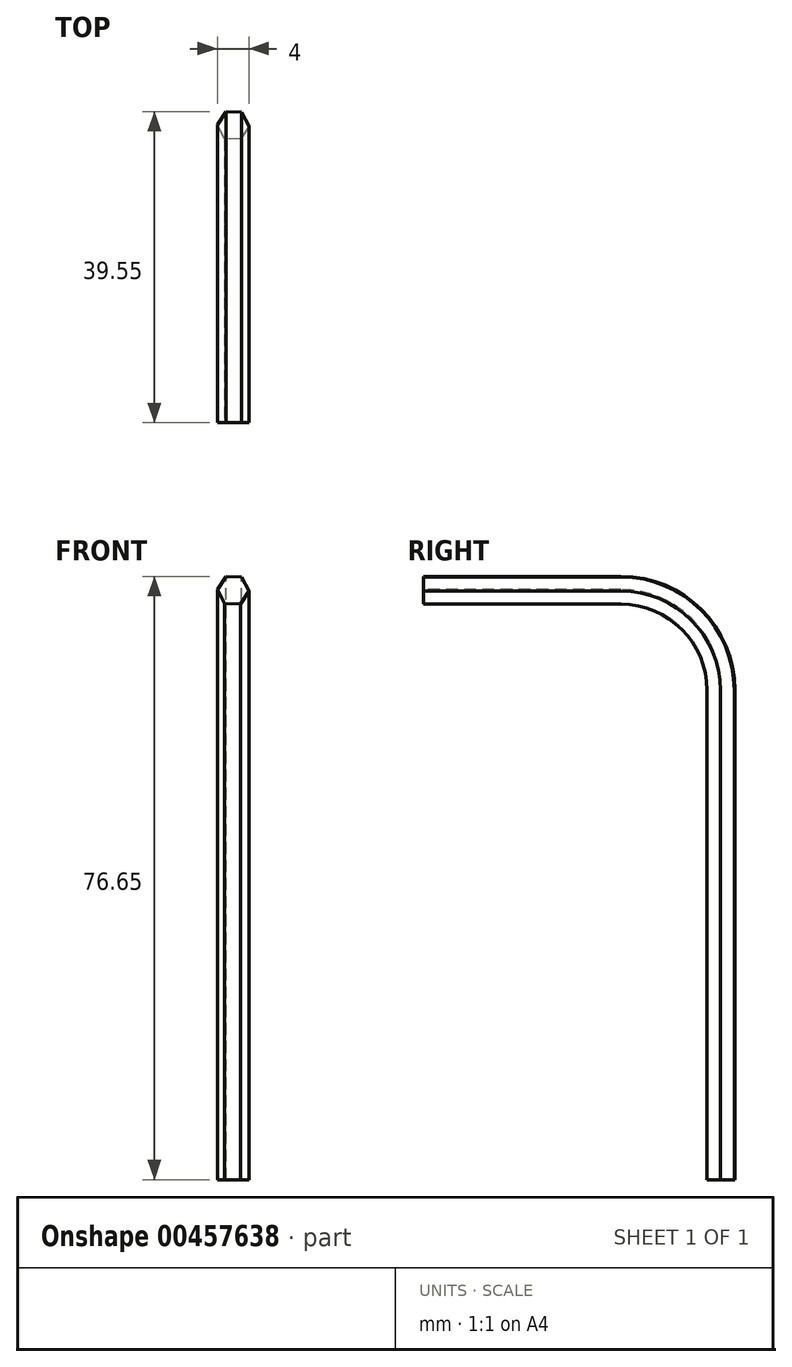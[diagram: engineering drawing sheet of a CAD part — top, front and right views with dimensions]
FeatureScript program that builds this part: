
annotation { "Feature Type Name" : "Feature", "Feature Type Description" : "" }
export const myFeature = defineFeature(function(context is Context, id is Id, definition is map)
    precondition{}
    {
        {
            var Q0;
            Q0=qCreatedBy(makeId("Top.planeOp"),FACE);
            var sketch = newSketch(context, id + "F0", { "sketchPlane" : qUnion([Q0])});
            skCircle(sketch, "E0.cCircle", {"center": v(0, 0) * mm, "radius": 1.73 * mm, "construction": true});
            skLineSegment(sketch, "E0.0", {"start": v(-1.07, -1.7) * mm, "end": v(-2, 0.08) * mm});
            skLineSegment(sketch, "E0.1", {"start": v(-2, 0.08) * mm, "end": v(-0.93, 1.77) * mm});
            skLineSegment(sketch, "E0.2", {"start": v(-0.93, 1.77) * mm, "end": v(1.07, 1.7) * mm});
            skLineSegment(sketch, "E0.3", {"start": v(1.07, 1.7) * mm, "end": v(2, -0.08) * mm});
            skLineSegment(sketch, "E0.4", {"start": v(2, -0.08) * mm, "end": v(0.93, -1.77) * mm});
            skLineSegment(sketch, "E0.5", {"start": v(0.93, -1.77) * mm, "end": v(-1.07, -1.7) * mm});
            skPoint(sketch, "E0.0.midPoint", {"position": v(-1.53, -0.8) * mm});
            skSolve(sketch);
        }
        {
            var Q0;
            Q0=qCreatedBy(makeId("Right.planeOp"),FACE);
            var sketch = newSketch(context, id + "F1", { "sketchPlane" : qUnion([Q0])});
            skLineSegment(sketch, "E1", {"start": v(0, 0) * mm, "end": v(0, 62.18) * mm});
            skLineSegment(sketch, "E2", {"start": v(-12.7, 74.88) * mm, "end": v(-37.78, 74.88) * mm});
            skPoint(sketch, "E3.visualSharp", {"position": v(0, 74.88) * mm});
            skArc(sketch, "E3.filletArc", {"start": v(0, 62.18) * mm, "mid": v(-3.72, 71.16) * mm, "end": v(-12.7, 74.88) * mm});
            skSolve(sketch);
        }
        {
            var Q0;
            Q0=makeQuery(id+"F0.imprint","IMPRINT",FACE,{"disambiguationData":[TD([[makeQuery(id+"F0.imprint","IMPRINT",EDGE,{"derivedFrom":sQuery(id+"F0.wireOp",EDGE,"E0.0")}),-1.0]])]});
            var Q1;
            Q1=sQuery(id+"F1.wireOp",EDGE,"E1");
            var Q2;
            Q2=sQuery(id+"F1.wireOp",EDGE,"E3.filletArc");
            var Q3;
            Q3=sQuery(id+"F1.wireOp",EDGE,"E2");
            sweep(context, id + "F2", {"profiles" : qUnion([Q0]), "path" : qUnion([Q1, Q2, Q3])});
        }
    });
